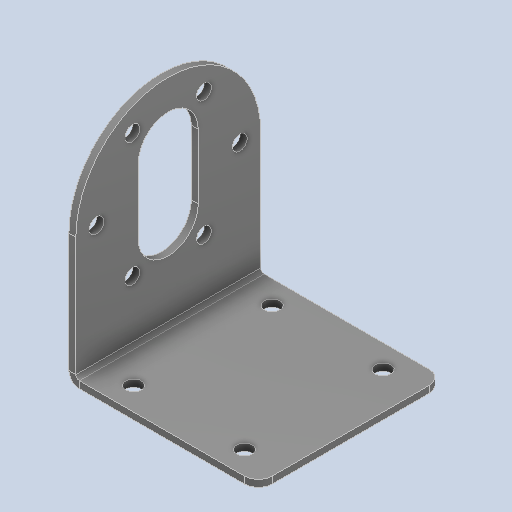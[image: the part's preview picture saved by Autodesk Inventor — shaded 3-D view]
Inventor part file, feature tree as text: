
AUTODESK INVENTOR PART (.ipt)
format: ipt  version: 2023 (Build 270158000, 158)  size: 148,480 bytes
history: mixed  units: in
note: dims shown in document units (in); Inventor stores cm internally (conversion verified against a paired STEP export)
features: fillet x1, imported_body x1
ambient origin geometry x8: Origin, YZ Plane, XZ Plane, XY Plane, X Axis, Y Axis, Z Axis, Center Point
bodies: Solid1 (imported_parasolid)
feature tree (2):
  fillet  "Fillet1"  [1 undecoded]
  imported_body  NMx_Import_Brep_tag  [imported B-rep: ~30 faces, bbox_mm=[41.0, 41.423394, 40.0]]
note: 1 required parameter value undecoded (feature->parameter linkage not recoverable at this tier; creation-order binding heuristic only, values carry confidence <= 0.55)
